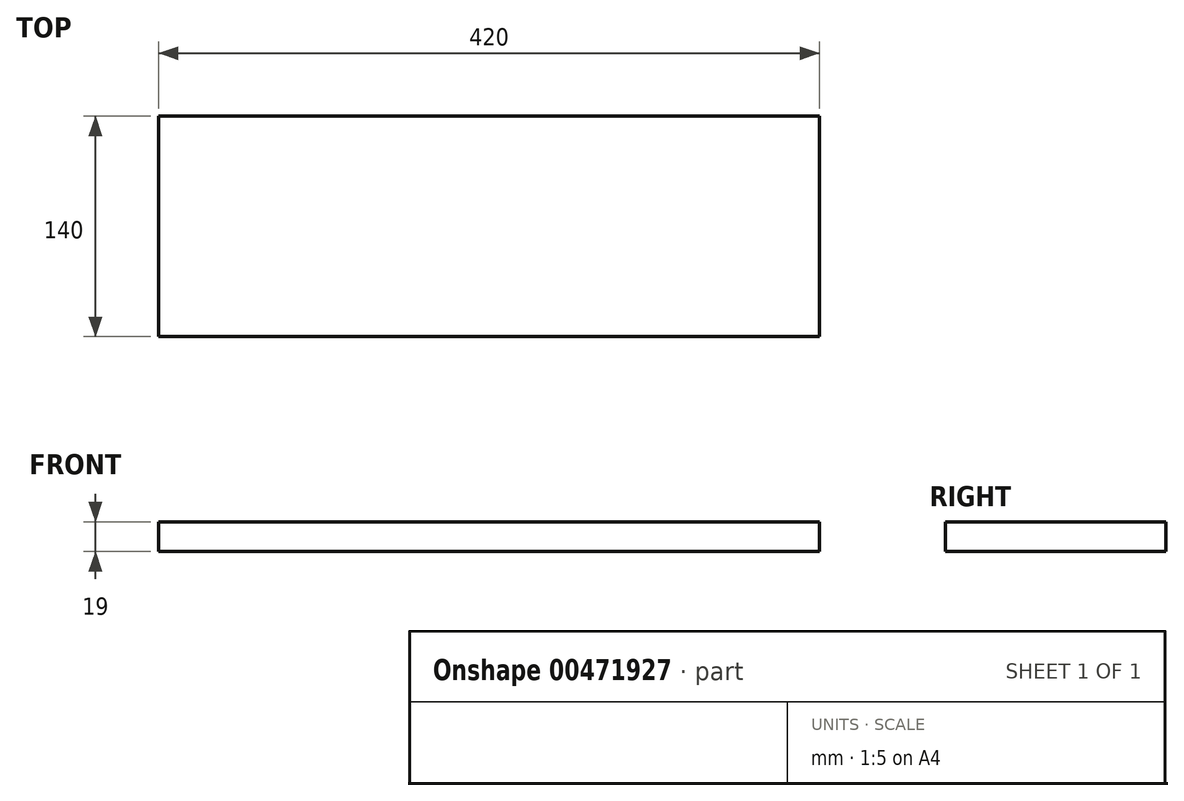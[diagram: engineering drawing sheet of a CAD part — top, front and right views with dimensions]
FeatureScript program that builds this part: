
annotation { "Feature Type Name" : "Feature", "Feature Type Description" : "" }
export const myFeature = defineFeature(function(context is Context, id is Id, definition is map)
    precondition{}
    {
        {
            var Q0;
            Q0=qCreatedBy(makeId("Top.planeOp"),FACE);
            var sketch = newSketch(context, id + "F0", { "sketchPlane" : qUnion([Q0])});
            skLineSegment(sketch, "E0", {"start": v(-52.46, -24.68) * mm, "end": v(-52.46, 115.32) * mm});
            skLineSegment(sketch, "E1", {"start": v(-52.46, 115.32) * mm, "end": v(367.54, 115.32) * mm});
            skLineSegment(sketch, "E2", {"start": v(367.54, 115.32) * mm, "end": v(367.54, -24.68) * mm});
            skLineSegment(sketch, "E3", {"start": v(367.54, -24.68) * mm, "end": v(-52.46, -24.68) * mm});
            skSolve(sketch);
        }
        {
            var Q0;
            Q0 = qSketchRegion(id + "F0", true);
            extrude(context, id + "F1", {"entities" : qUnion([Q0]), "depth" : 19 * mm});
        }
    });
